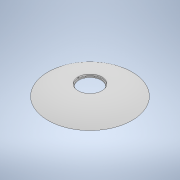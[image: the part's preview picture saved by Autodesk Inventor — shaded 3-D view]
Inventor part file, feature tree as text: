
AUTODESK INVENTOR PART (.ipt)
format: ipt  version: 2020 (Build 240168000, 168)  size: 175,104 bytes
history: native  units: mm
features: sketch x3, extrude x2, revolve x1, shell x1, plane x1, pattern_circular x1
ambient origin geometry x8: Origin, YZ Plane, XZ Plane, XY Plane, X Axis, Y Axis, Z Axis, Center Point
bodies: Solid1 (feature_tree)
feature tree (9):
  revolve  "Revolution1"  [1 undecoded]
  shell  "Shell1"  Thickness=140.0mm
  extrude  "Extrusion1"  Depth=3.0mm
  plane  "Work Plane1"
  extrude  "Extrusion2"  Depth=2.0mm TaperAngle=0.0deg
  pattern_circular  "Circular Pattern1"  [2 undecoded]
  sketch  "Sketch1"  dims[d0=40.0mm d1=5.0mm d2=140.0mm]
  sketch  "Sketch2"  dims[d3=90.0deg d4=3.0mm]
  sketch  "Sketch4"  dims[d5=74.0mm d6=1.507mm d7=0.0mm d8=2.0mm d9=2.0mm d10=1.5mm d11=2.0mm d12=0.0mm d13=20.0mm d14=360.0deg]
note: 3 required parameter values undecoded (feature->parameter linkage not recoverable at this tier; creation-order binding heuristic only, values carry confidence <= 0.55)